annotation { "Feature Type Name" : "Feature", "Feature Type Description" : "" }
export const myFeature = defineFeature(function(context is Context, id is Id, definition is map)
    precondition{}
    {
        {
            var Q0;
            Q0=qCreatedBy(makeId("Front.planeOp"),FACE);
            var sketch = newSketch(context, id + "F0", { "sketchPlane" : qUnion([Q0])});
            skLineSegment(sketch, "E0.top", {"start": v(0, -101.6) * mm, "end": v(-101.6, -101.6) * mm});
            skLineSegment(sketch, "E0.left", {"start": v(0, 0) * mm, "end": v(0, -101.6) * mm});
            skLineSegment(sketch, "E0.right", {"start": v(-101.6, 0) * mm, "end": v(-101.6, -101.6) * mm});
            skArc(sketch, "E1", {"start": v(0, 0) * mm, "mid": v(-50.8, 50.8) * mm, "end": v(-101.6, 0) * mm});
            skSolve(sketch);
        }
        {
            var Q0;
            Q0=makeQuery(id+"F0.imprint","IMPRINT",FACE,{"disambiguationData":[TD([[makeQuery(id+"F0.imprint","IMPRINT",EDGE,{"derivedFrom":sQuery(id+"F0.wireOp",EDGE,"E0.top")}),-1.0]])]});
            extrude(context, id + "F1", {"entities" : qUnion([Q0]), "depth" : 17.78 * mm});
        }
        {
            var Q0;
            Q0=makeQuery(id+"F1.opExtrude","CAP_FACE",FACE,{"disambiguationData":[OSD([sQuery(id+"F0.wireOp",EDGE,"E0.top"),sQuery(id+"F0.wireOp",EDGE,"E0.left"),sQuery(id+"F0.wireOp",EDGE,"E0.right"),sQuery(id+"F0.wireOp",EDGE,"E1")])],"isStart":false});
            var sketch = newSketch(context, id + "F2", { "sketchPlane" : qUnion([Q0])});
            skLineSegment(sketch, "E2", {"start": v(0, 0) * mm, "end": v(-119.38, 0) * mm, "construction": true});
            skLineSegment(sketch, "E3", {"start": v(-50.8, 50.8) * mm, "end": v(-50.8, 34.37) * mm, "construction": true});
            skLineSegment(sketch, "E4.bottom", {"start": v(-54.6, 41.8) * mm, "end": v(-47.69, 41.8) * mm});
            skLineSegment(sketch, "E4.top", {"start": v(-54.6, 9.52) * mm, "end": v(-47.69, 9.52) * mm});
            skLineSegment(sketch, "E4.left", {"start": v(-54.6, 41.8) * mm, "end": v(-54.6, 34.37) * mm});
            skLineSegment(sketch, "E4.right", {"start": v(-47.69, 41.8) * mm, "end": v(-47.69, 34.37) * mm});
            skLineSegment(sketch, "E5.bottom", {"start": v(-63.82, 34.37) * mm, "end": v(-54.6, 34.37) * mm});
            skLineSegment(sketch, "E5.top", {"start": v(-63.82, 28.47) * mm, "end": v(-54.6, 28.47) * mm});
            skLineSegment(sketch, "E5.left", {"start": v(-63.82, 34.37) * mm, "end": v(-63.82, 28.47) * mm});
            skLineSegment(sketch, "E5.right", {"start": v(-38.72, 34.37) * mm, "end": v(-38.72, 28.47) * mm});
            skLineSegment(sketch, "E6.trimOffspring", {"start": v(-54.6, 28.47) * mm, "end": v(-54.6, 9.52) * mm});
            skLineSegment(sketch, "E7.trimOffspring", {"start": v(-47.69, 28.47) * mm, "end": v(-47.69, 9.52) * mm});
            skLineSegment(sketch, "E8.trimOffspring", {"start": v(-50.8, 28.47) * mm, "end": v(-50.8, -101.6) * mm, "construction": true});
            skLineSegment(sketch, "E9.trimOffspring", {"start": v(-47.69, 34.37) * mm, "end": v(-38.72, 34.37) * mm});
            skLineSegment(sketch, "E10.trimOffspring", {"start": v(-47.69, 28.47) * mm, "end": v(-38.72, 28.47) * mm});
            skText(sketch, "E11", { "text": "Angelica Posh\n\n", "fontName": "OpenSans-Regular.ttf"});
            skText(sketch, "E12", { "text": "1999 - ", "fontName": "OpenSans-Regular.ttf"});
            const initialGuessF2  = {"E11": [-0.09582, -0.01822, 1, 0, 0.0099], "E12": [-0.0845, -0.03923, 1, 0, 0.01007]};
            skSetInitialGuess(sketch, initialGuessF2);
            skSolve(sketch);
        }
        {
            var Q0;
            Q0 = qSketchRegion(id + "F2", true);
            extrude(context, id + "F3", {"entities" : qUnion([Q0]), "operationType" : NewBodyOperationType.ADD, "depth" : 3.56 * mm});
        }
    });